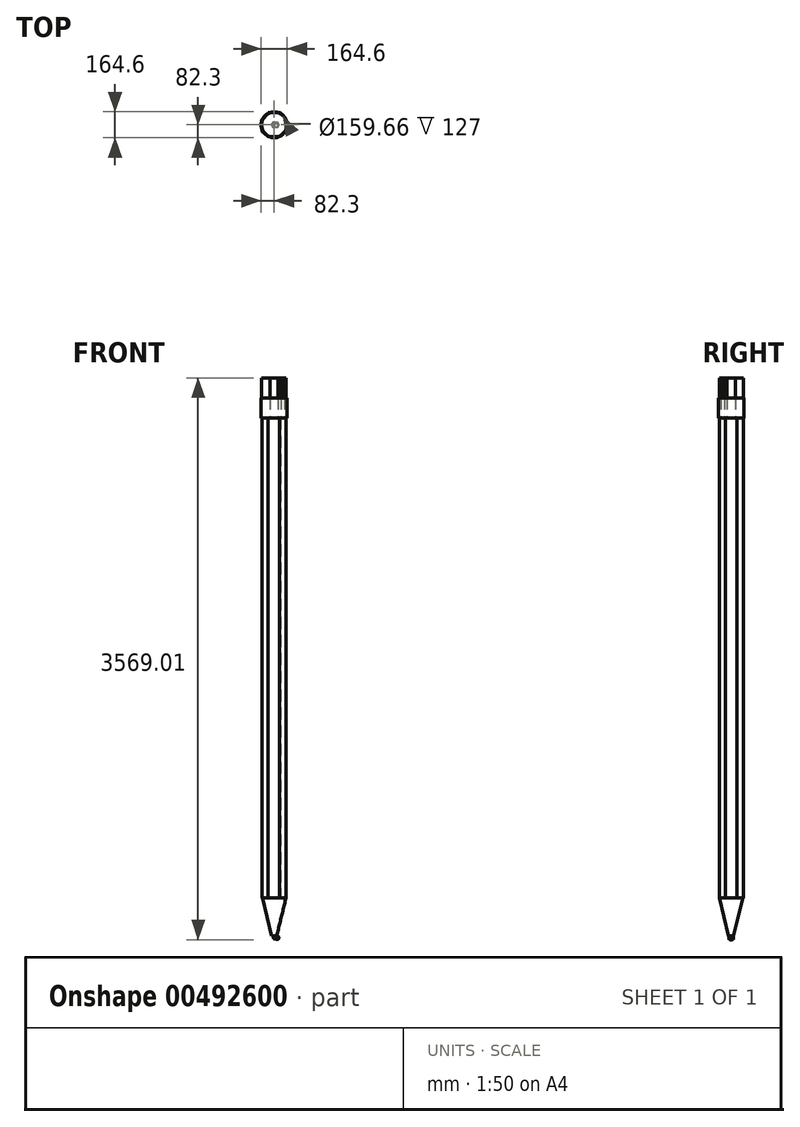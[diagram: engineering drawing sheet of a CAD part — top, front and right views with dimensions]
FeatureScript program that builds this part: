
annotation { "Feature Type Name" : "Feature", "Feature Type Description" : "" }
export const myFeature = defineFeature(function(context is Context, id is Id, definition is map)
    precondition{}
    {
        {
            var Q0;
            Q0=qCreatedBy(makeId("Top.planeOp"),FACE);
            var sketch = newSketch(context, id + "F0", { "sketchPlane" : qUnion([Q0])});
            skLineSegment(sketch, "E0", {"start": v(-37.72, 76.35) * mm, "end": v(40.28, 76.35) * mm});
            skLineSegment(sketch, "E1", {"start": v(40.28, 76.35) * mm, "end": v(75.43, 34.97) * mm});
            skLineSegment(sketch, "E2", {"start": v(75.43, 34.97) * mm, "end": v(75.43, -34.97) * mm});
            skLineSegment(sketch, "E3", {"start": v(75.43, -34.97) * mm, "end": v(35.15, -75.62) * mm});
            skLineSegment(sketch, "E4", {"start": v(35.15, -75.62) * mm, "end": v(-37.72, -75.62) * mm});
            skLineSegment(sketch, "E5", {"start": v(-37.72, -75.62) * mm, "end": v(-76.53, -41.93) * mm});
            skLineSegment(sketch, "E6", {"start": v(-76.53, -41.93) * mm, "end": v(-76.53, 31.3) * mm});
            skLineSegment(sketch, "E7", {"start": v(-76.53, 31.3) * mm, "end": v(-37.72, 76.35) * mm});
            skSolve(sketch);
        }
        {
            var Q0;
            Q0=makeQuery(id+"F0.imprint","IMPRINT",FACE,{"disambiguationData":[TD([[makeQuery(id+"F0.imprint","IMPRINT",EDGE,{"derivedFrom":sQuery(id+"F0.wireOp",EDGE,"E0")}),-1.0]])]});
            extrude(context, id + "F1", {"entities" : qUnion([Q0]), "depth" : 3048 * mm});
        }
        {
            var Q0;
            Q0=makeQuery(id+"F1.opExtrude","CAP_FACE",FACE,{"disambiguationData":[OSD([sQuery(id+"F0.wireOp",EDGE,"E0"),sQuery(id+"F0.wireOp",EDGE,"E1"),sQuery(id+"F0.wireOp",EDGE,"E2"),sQuery(id+"F0.wireOp",EDGE,"E3"),sQuery(id+"F0.wireOp",EDGE,"E4"),sQuery(id+"F0.wireOp",EDGE,"E5"),sQuery(id+"F0.wireOp",EDGE,"E6"),sQuery(id+"F0.wireOp",EDGE,"E7")])],"isStart":false});
            var sketch = newSketch(context, id + "F2", { "sketchPlane" : qUnion([Q0])});
            skCircle(sketch, "E8", {"center": v(0, 0) * mm, "radius": 79.83 * mm});
            skCircle(sketch, "E9", {"center": v(0, 0) * mm, "radius": 82.3 * mm});
            skSolve(sketch);
        }
        {
            var Q0;
            Q0 = qSketchRegion(id + "F2", true);
            var Q1;
            Q1=sQuery(id+"F2.wireOp",EDGE,"E8");
            extrude(context, id + "F3", {"entities" : qUnion([Q0]), "surfaceEntities" : qUnion([Q1]), "depth" : 127 * mm});
        }
        {
            var Q0;
            {var subQ0=sQuery(id+"F2.wireOp",EDGE,"E8");var subQ1=makeQuery(id+"F1.opExtrude","CAP_EDGE",EDGE,{"disambiguationData":[OSD([sQuery(id+"F0.wireOp",EDGE,"E6")])],"isStart":false});var subQ2=makeQuery(id+"F2.imprint","INTERSECT",VERTEX,{"disambiguationData":[OD(0.0)],"derivedFrom":[subQ1,subQ0]});Q0=makeQuery(id+"F2.imprint","IMPRINT",FACE,{"disambiguationData":[TD([[makeQuery(id+"F2.imprint","IMPRINT",EDGE,{"disambiguationData":[TD([[subQ2,-1.0]])],"derivedFrom":subQ0}),1.0]])]});}
            var Q1;
            {var subQ0=sQuery(id+"F2.wireOp",EDGE,"E8");var subQ4=makeQuery(id+"F1.opExtrude","CAP_EDGE",EDGE,{"disambiguationData":[OSD([sQuery(id+"F0.wireOp",EDGE,"E0")])],"isStart":false});var subQ8=makeQuery(id+"F2.imprint","INTERSECT",VERTEX,{"disambiguationData":[OD(0.0)],"derivedFrom":[subQ4,subQ0]});Q1=makeQuery(id+"F2.imprint","IMPRINT",FACE,{"disambiguationData":[TD([[makeQuery(id+"F2.imprint","IMPRINT",EDGE,{"disambiguationData":[TD([[subQ8,1.0]])],"derivedFrom":subQ0}),1.0]])]});}
            extrude(context, id + "F4", {"entities" : qUnion([Q0, Q1]), "depth" : 254 * mm});
        }
        {
            var Q0;
            Q0=qCreatedBy(makeId("Front.planeOp"),FACE);
            var sketch = newSketch(context, id + "F5", { "sketchPlane" : qUnion([Q0])});
            skLineSegment(sketch, "E10", {"start": v(0, 0) * mm, "end": v(0, -243.85) * mm});
            skLineSegment(sketch, "E11", {"start": v(75.42, 0) * mm, "end": v(0, 0) * mm});
            skLineSegment(sketch, "E12", {"start": v(16, -243.85) * mm, "end": v(0, -243.85) * mm});
            skLineSegment(sketch, "E13", {"start": v(75.42, 0) * mm, "end": v(16, -243.85) * mm});
            skSolve(sketch);
        }
        {
            var Q0;
            Q0=makeQuery(id+"F5.imprint","IMPRINT",FACE,{"disambiguationData":[TD([[makeQuery(id+"F5.imprint","IMPRINT",EDGE,{"derivedFrom":sQuery(id+"F5.wireOp",EDGE,"E10")}),1.0]])]});
            var Q1;
            Q1=sQuery(id+"F5.wireOp",EDGE,"E10");
            revolve(context, id + "F6", {"operationType" : NewBodyOperationType.ADD, "entities" : qUnion([Q0]), "axis" : qUnion([Q1]), "revolveType" : RevolveType.FULL});
        }
        {
            var Q0;
            Q0=qCreatedBy(makeId("Front.planeOp"),FACE);
            var sketch = newSketch(context, id + "F7", { "sketchPlane" : qUnion([Q0])});
            skLineSegment(sketch, "E14", {"start": v(75.42, 0) * mm, "end": v(16, -243.85) * mm});
            skLineSegment(sketch, "E15.0", {"start": v(-16, -243.85) * mm, "end": v(16, -243.85) * mm});
            skLineSegment(sketch, "E16", {"start": v(16, -243.85) * mm, "end": v(11.2, -263.56) * mm});
            skLineSegment(sketch, "E17", {"start": v(11.2, -263.56) * mm, "end": v(-2.96, -260.11) * mm});
            skLineSegment(sketch, "E18", {"start": v(-2.96, -260.11) * mm, "end": v(0, -243.85) * mm});
            skLineSegment(sketch, "E19", {"start": v(0, -243.85) * mm, "end": v(16, -243.85) * mm});
            skSolve(sketch);
        }
        {
            var Q0;
            Q0=makeQuery(id+"F7.imprint","IMPRINT",FACE,{"disambiguationData":[TD([[makeQuery(id+"F7.imprint","IMPRINT",EDGE,{"derivedFrom":sQuery(id+"F7.wireOp",EDGE,"E16")}),-1.0]])]});
            var Q1;
            Q1=sQuery(id+"F7.wireOp",EDGE,"E16");
            revolve(context, id + "F8", {"operationType" : NewBodyOperationType.ADD, "entities" : qUnion([Q0]), "axis" : qUnion([Q1]), "revolveType" : RevolveType.FULL});
        }
    });
